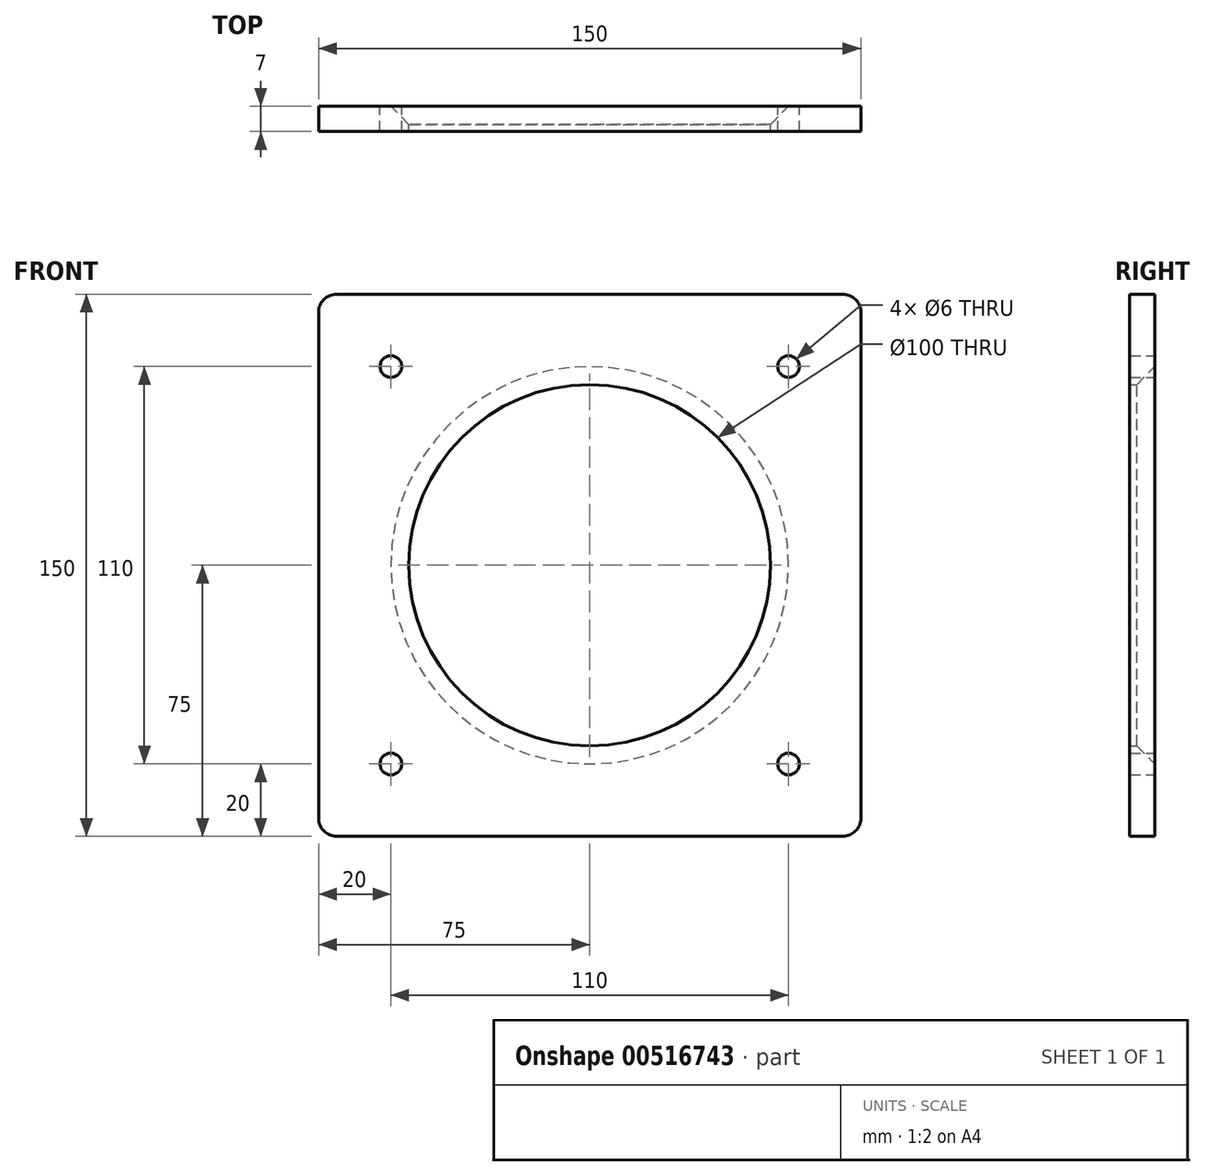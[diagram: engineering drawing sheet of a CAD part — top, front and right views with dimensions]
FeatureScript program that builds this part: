
annotation { "Feature Type Name" : "Feature", "Feature Type Description" : "" }
export const myFeature = defineFeature(function(context is Context, id is Id, definition is map)
    precondition{}
    {
        {
            var Q0;
            Q0=qCreatedBy(makeId("Front.planeOp"),FACE);
            var sketch = newSketch(context, id + "F0", { "sketchPlane" : qUnion([Q0])});
            skCircle(sketch, "E0", {"center": v(0, 0) * mm, "radius": 50 * mm});
            skCircle(sketch, "E1", {"center": v(-55, 55) * mm, "radius": 3 * mm});
            skCircle(sketch, "E2", {"center": v(55, 55) * mm, "radius": 3 * mm});
            skCircle(sketch, "E3", {"center": v(55, -55) * mm, "radius": 3 * mm});
            skCircle(sketch, "E4", {"center": v(-55, -55) * mm, "radius": 3 * mm});
            skLineSegment(sketch, "E5.bottom", {"start": v(-75, 75) * mm, "end": v(75, 75) * mm});
            skLineSegment(sketch, "E5.top", {"start": v(-75, -75) * mm, "end": v(75, -75) * mm});
            skLineSegment(sketch, "E5.left", {"start": v(-75, 75) * mm, "end": v(-75, -75) * mm});
            skLineSegment(sketch, "E5.right", {"start": v(75, 75) * mm, "end": v(75, -75) * mm});
            skSolve(sketch);
        }
        {
            var Q0;
            Q0=qSketchRegion(id+"F0",true);
            extrude(context, id + "F1", {"entities" : qUnion([Q0]), "depth" : 7 * mm, "offsetDistance" : 25 * mm});
        }
        {
            var Q0;
            Q0=makeQuery(id+"F1.opExtrude","CAP_EDGE",EDGE,{"disambiguationData":[OSD([sQuery(id+"F0.wireOp",EDGE,"E0")])],"isStart":true});
            chamfer(context, id + "F2", {"entities" : qUnion([Q0]), "chamferType" : ChamferType.OFFSET_ANGLE, "width" : 5 * mm, "oppositeDirection" : false, "angle" : 45 * degree, "tangentPropagation" : true});
        }
        {
            var Q0;
            Q0=makeQuery(id+"F1.opExtrude","SWEPT_EDGE",EDGE,{"disambiguationData":[OSD([sQuery(id+"F0.wireOp",EDGE,"E5.bottom"),sQuery(id+"F0.wireOp",EDGE,"E5.right")])]});
            var Q1;
            Q1=makeQuery(id+"F1.opExtrude","SWEPT_EDGE",EDGE,{"disambiguationData":[OSD([sQuery(id+"F0.wireOp",EDGE,"E5.bottom"),sQuery(id+"F0.wireOp",EDGE,"E5.left")])]});
            var Q2;
            Q2=makeQuery(id+"F1.opExtrude","SWEPT_EDGE",EDGE,{"disambiguationData":[OSD([sQuery(id+"F0.wireOp",EDGE,"E5.top"),sQuery(id+"F0.wireOp",EDGE,"E5.left")])]});
            var Q3;
            Q3=makeQuery(id+"F1.opExtrude","SWEPT_EDGE",EDGE,{"disambiguationData":[OSD([sQuery(id+"F0.wireOp",EDGE,"E5.top"),sQuery(id+"F0.wireOp",EDGE,"E5.right")])]});
            fillet(context, id + "F3", {"entities" : qUnion([Q0, Q1, Q2, Q3]), "radius" : 5 * mm, "tangentPropagation" : true, "allowEdgeOverflow" : false});
        }
    });
